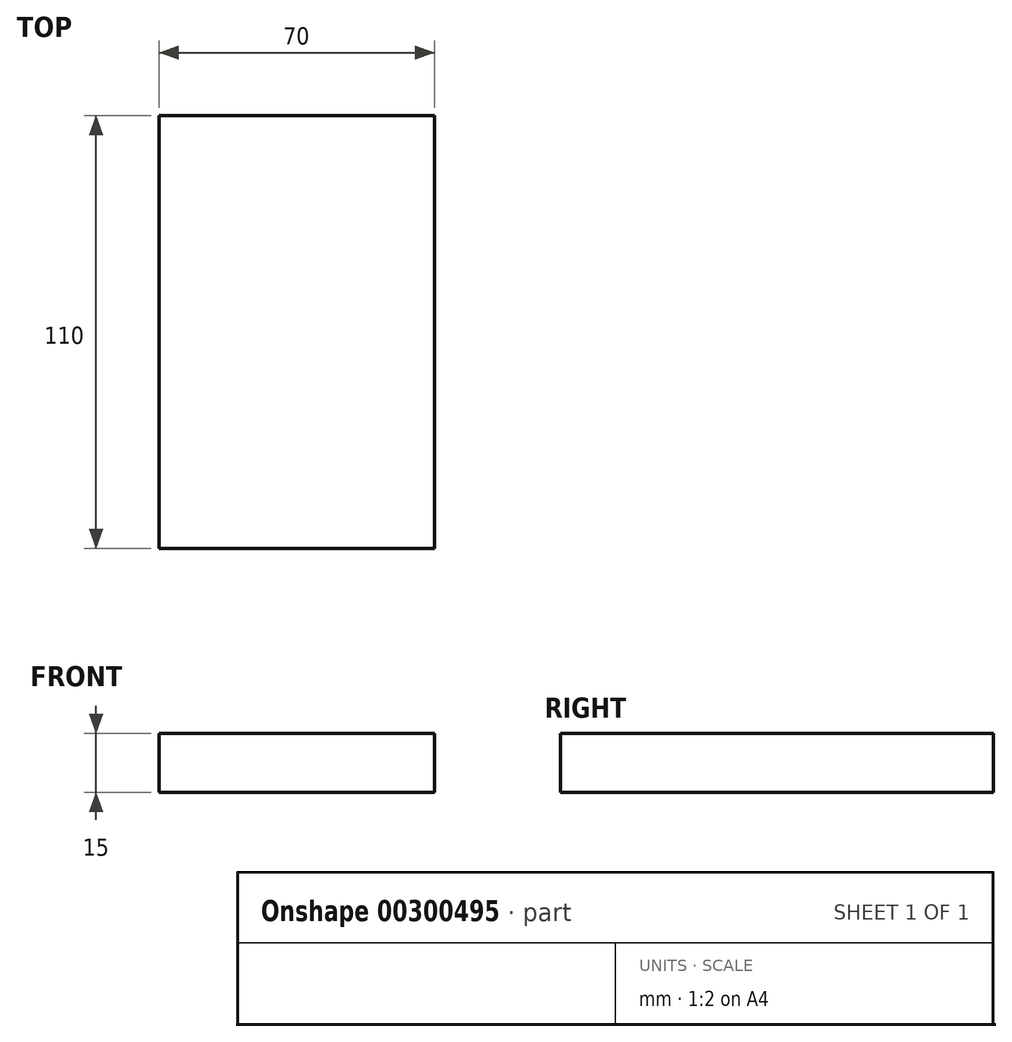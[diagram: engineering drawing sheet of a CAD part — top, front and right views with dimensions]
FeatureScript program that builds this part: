
annotation { "Feature Type Name" : "Feature", "Feature Type Description" : "" }
export const myFeature = defineFeature(function(context is Context, id is Id, definition is map)
    precondition{}
    {
        {
            var Q0;
            Q0=qCreatedBy(makeId("Top.planeOp"),FACE);
            var sketch = newSketch(context, id + "F0", { "sketchPlane" : qUnion([Q0])});
            skLineSegment(sketch, "E0.bottom", {"start": v(35, 55) * mm, "end": v(-35, 55) * mm});
            skLineSegment(sketch, "E0.top", {"start": v(35, -55) * mm, "end": v(-35, -55) * mm});
            skLineSegment(sketch, "E0.left", {"start": v(35, 55) * mm, "end": v(35, -55) * mm});
            skLineSegment(sketch, "E0.right", {"start": v(-35, 55) * mm, "end": v(-35, -55) * mm});
            skPoint(sketch, "E0.middle", {"position": v(0, 0) * mm});
            skSolve(sketch);
        }
        {
            var Q0;
            Q0 = qSketchRegion(id + "F0", true);
            extrude(context, id + "F1", {"entities" : qUnion([Q0]), "depth" : 15 * mm});
        }
    });
